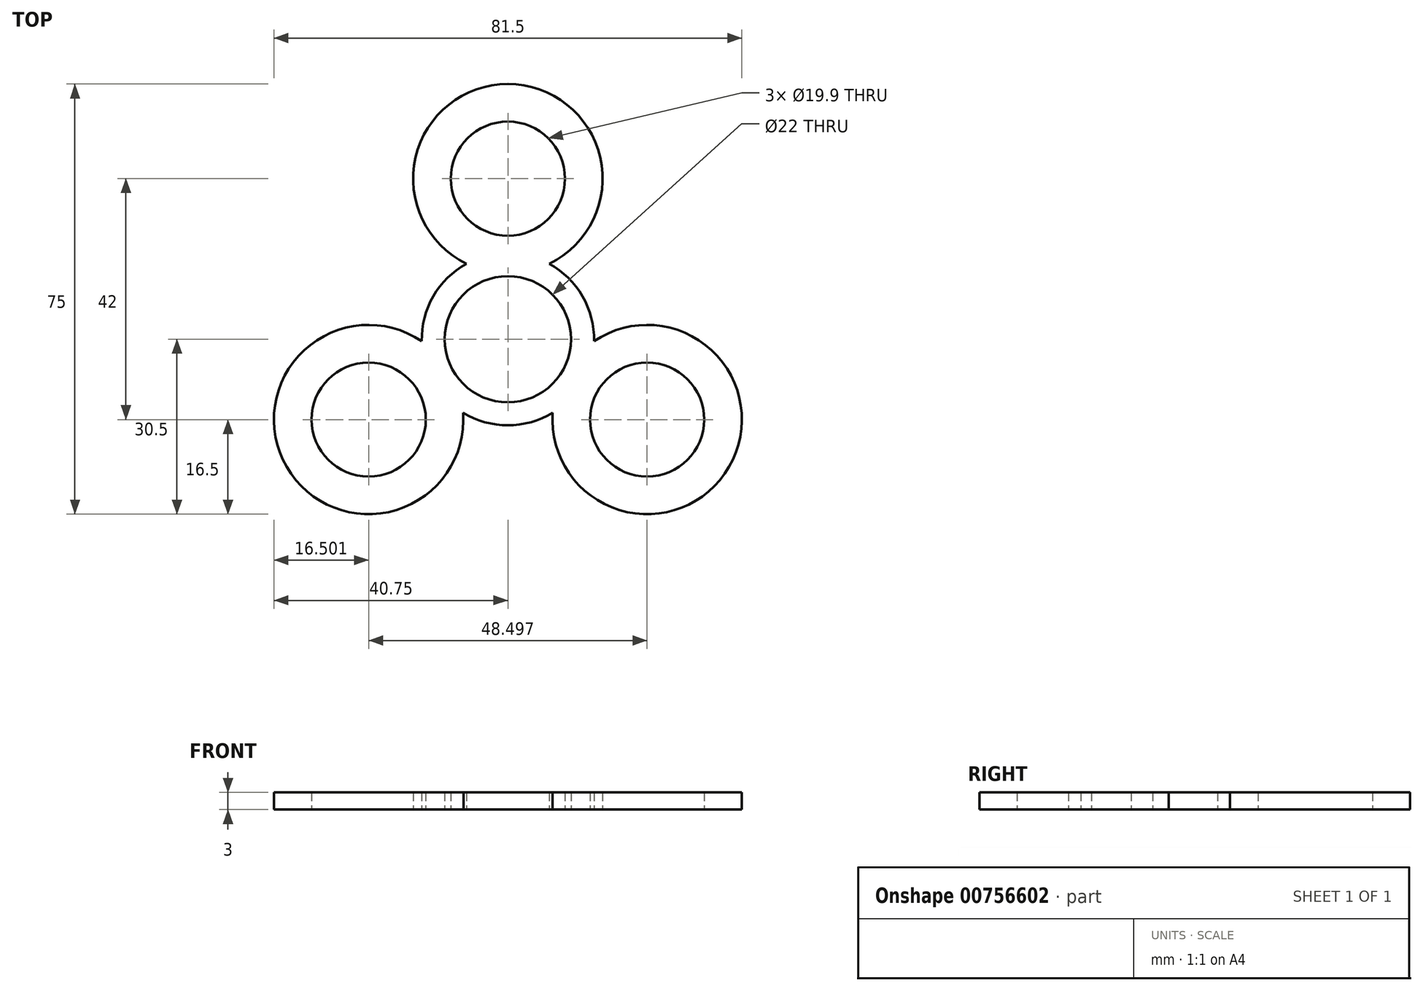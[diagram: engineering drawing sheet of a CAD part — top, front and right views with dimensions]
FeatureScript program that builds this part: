
annotation { "Feature Type Name" : "Feature", "Feature Type Description" : "" }
export const myFeature = defineFeature(function(context is Context, id is Id, definition is map)
    precondition{}
    {
        {
            var Q0;
            Q0=qCreatedBy(makeId("Top.planeOp"),FACE);
            var sketch = newSketch(context, id + "F0", { "sketchPlane" : qUnion([Q0])});
            skArc(sketch, "E0", {"start": v(9.53, 5.5) * mm, "mid": v(0, 11) * mm, "end": v(-9.53, 5.5) * mm});
            skCircle(sketch, "E1", {"center": v(0, 28) * mm, "radius": 9.95 * mm});
            skLineSegment(sketch, "E2", {"start": v(0, 28) * mm, "end": v(0, 0) * mm});
            skArc(sketch, "E3", {"start": v(-7.2, 13.16) * mm, "mid": v(-10.49, 10.73) * mm, "end": v(-13, 7.5) * mm});
            skArc(sketch, "E4", {"start": v(7.2, 13.16) * mm, "mid": v(0, 44.5) * mm, "end": v(-7.2, 13.16) * mm});
            skArc(sketch, "E5.trimOffspring", {"start": v(13, 7.5) * mm, "mid": v(10.49, 10.73) * mm, "end": v(7.2, 13.16) * mm});
            skArc(sketch, "E6.1.0", {"start": v(7.8, -12.82) * mm, "mid": v(38.54, -22.25) * mm, "end": v(15, -0.34) * mm});
            skCircle(sketch, "E6.1.1", {"center": v(24.25, -14) * mm, "radius": 9.95 * mm});
            skArc(sketch, "E6.1.2", {"start": v(15, -0.34) * mm, "mid": v(14.53, 3.72) * mm, "end": v(13, 7.5) * mm});
            skArc(sketch, "E6.1.3", {"start": v(0, -15) * mm, "mid": v(4.05, -14.44) * mm, "end": v(7.8, -12.82) * mm});
            skArc(sketch, "E6.1.4", {"start": v(0, -11) * mm, "mid": v(9.53, -5.5) * mm, "end": v(9.53, 5.5) * mm});
            skArc(sketch, "E6.2.0", {"start": v(-15, -0.34) * mm, "mid": v(-38.54, -22.25) * mm, "end": v(-7.8, -12.82) * mm});
            skCircle(sketch, "E6.2.1", {"center": v(-24.25, -14) * mm, "radius": 9.95 * mm});
            skArc(sketch, "E6.2.2", {"start": v(-7.8, -12.82) * mm, "mid": v(-4.05, -14.44) * mm, "end": v(0, -15) * mm});
            skArc(sketch, "E6.2.3", {"start": v(-13, 7.5) * mm, "mid": v(-14.53, 3.72) * mm, "end": v(-15, -0.34) * mm});
            skArc(sketch, "E6.2.4", {"start": v(-9.53, 5.5) * mm, "mid": v(-9.53, -5.5) * mm, "end": v(0, -11) * mm});
            skLineSegment(sketch, "E6.anchor1", {"start": v(0, 0) * mm, "end": v(-7.2, 13.16) * mm, "construction": true});
            skLineSegment(sketch, "E6.anchor2", {"start": v(0, 0) * mm, "end": v(-7.8, -12.82) * mm, "construction": true});
            skSolve(sketch);
        }
        {
            var Q0;
            Q0=makeQuery(id+"F0.imprint","IMPRINT",FACE,{"disambiguationData":[TD([[makeQuery(id+"F0.imprint","IMPRINT",EDGE,{"derivedFrom":sQuery(id+"F0.wireOp",EDGE,"E1")}),-1.0]])]});
            extrude(context, id + "F1", {"entities" : qUnion([Q0]), "depth" : 3 * mm, "offsetDistance" : 25 * mm});
        }
    });
